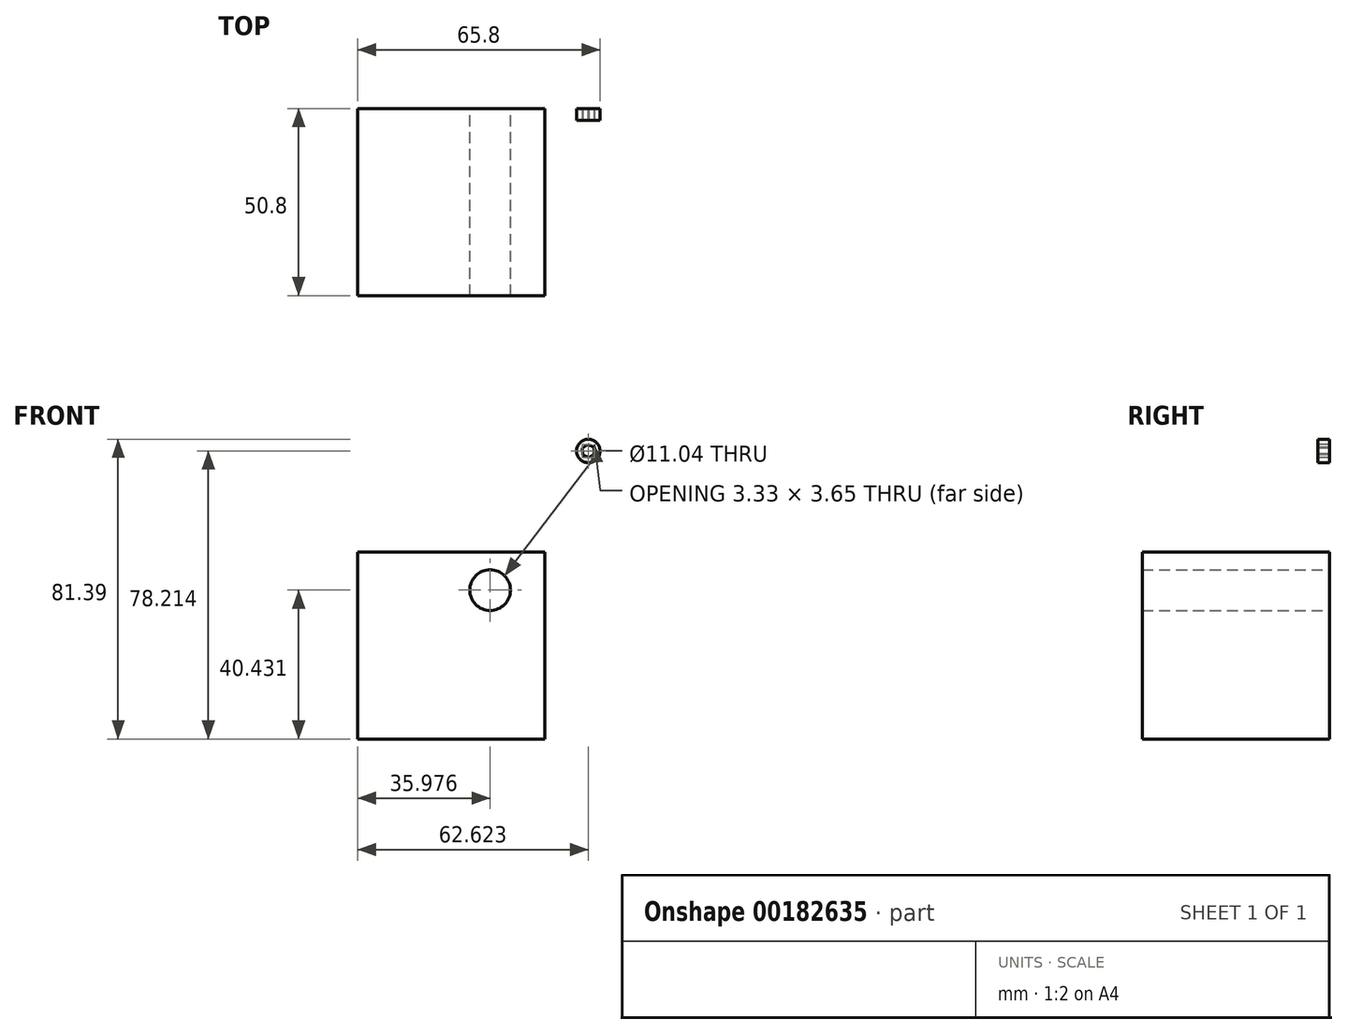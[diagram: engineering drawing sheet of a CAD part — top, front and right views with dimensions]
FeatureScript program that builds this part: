
annotation { "Feature Type Name" : "Feature", "Feature Type Description" : "" }
export const myFeature = defineFeature(function(context is Context, id is Id, definition is map)
    precondition{}
    {
        {
            var Q0;
            Q0=qCreatedBy(makeId("Front.planeOp"),FACE);
            var sketch = newSketch(context, id + "F0", { "sketchPlane" : qUnion([Q0])});
            skLineSegment(sketch, "E0", {"start": v(-24.42, 20.26) * mm, "end": v(26.38, 20.26) * mm});
            skLineSegment(sketch, "E1", {"start": v(26.38, 20.26) * mm, "end": v(26.38, -30.54) * mm});
            skLineSegment(sketch, "E2", {"start": v(26.38, -30.54) * mm, "end": v(-24.42, -30.54) * mm});
            skLineSegment(sketch, "E3", {"start": v(-24.42, 20.26) * mm, "end": v(-24.42, -30.54) * mm});
            skSolve(sketch);
        }
        {
            var Q0;
            Q0=makeQuery(id+"F0.imprint","IMPRINT",FACE,{"disambiguationData":[TD([[makeQuery(id+"F0.imprint","IMPRINT",EDGE,{"derivedFrom":sQuery(id+"F0.wireOp",EDGE,"E0")}),-1.0]])]});
            extrude(context, id + "F1", {"entities" : qUnion([Q0]), "depth" : 50.8 * mm});
        }
        {
            var Q0;
            Q0=makeQuery(id+"F0.imprint","IMPRINT",FACE,{"disambiguationData":[TD([[makeQuery(id+"F0.imprint","IMPRINT",EDGE,{"derivedFrom":sQuery(id+"F0.wireOp",EDGE,"E0")}),-1.0]])]});
            var sketch = newSketch(context, id + "F2", { "sketchPlane" : qUnion([Q0])});
            skCircle(sketch, "E4", {"center": v(11.56, 9.9) * mm, "radius": 5.52 * mm});
            skSolve(sketch);
        }
        {
            var Q0;
            Q0=makeQuery(id+"F2.imprint","IMPRINT",FACE,{"disambiguationData":[TD([[makeQuery(id+"F2.imprint","IMPRINT",EDGE,{"derivedFrom":sQuery(id+"F2.wireOp",EDGE,"E4")}),1.0]])]});
            extrude(context, id + "F3", {"entities" : qUnion([Q0]), "operationType" : NewBodyOperationType.REMOVE, "depth" : 50.8 * mm});
        }
        {
            var Q0;
            Q0=qCreatedBy(makeId("Front.planeOp"),FACE);
            var sketch = newSketch(context, id + "F4", { "sketchPlane" : qUnion([Q0])});
            skCircle(sketch, "E5", {"center": v(38.2, 47.67) * mm, "radius": 3.18 * mm});
            skSolve(sketch);
        }
        {
            var Q0;
            Q0=makeQuery(id+"F4.imprint","IMPRINT",FACE,{"disambiguationData":[TD([[makeQuery(id+"F4.imprint","IMPRINT",EDGE,{"derivedFrom":sQuery(id+"F4.wireOp",EDGE,"E5")}),1.0]])]});
            extrude(context, id + "F5", {"entities" : qUnion([Q0]), "depth" : 3.17 * mm});
        }
        {
            var Q0;
            Q0=makeQuery(id+"F5.opExtrude","CAP_FACE",FACE,{"disambiguationData":[OSD([sQuery(id+"F4.wireOp",EDGE,"E5")])],"isStart":false});
            var sketch = newSketch(context, id + "F6", { "sketchPlane" : qUnion([Q0])});
            skCircle(sketch, "E6.cCircle", {"center": v(38.2, 47.67) * mm, "radius": 1.59 * mm, "construction": true});
            skLineSegment(sketch, "E6.0", {"start": v(39.87, 46.91) * mm, "end": v(38.37, 45.85) * mm});
            skLineSegment(sketch, "E6.1", {"start": v(38.37, 45.85) * mm, "end": v(36.7, 46.61) * mm});
            skLineSegment(sketch, "E6.2", {"start": v(36.7, 46.61) * mm, "end": v(36.54, 48.44) * mm});
            skLineSegment(sketch, "E6.3", {"start": v(36.54, 48.44) * mm, "end": v(38.03, 49.5) * mm});
            skLineSegment(sketch, "E6.4", {"start": v(38.03, 49.5) * mm, "end": v(39.7, 48.74) * mm});
            skLineSegment(sketch, "E6.5", {"start": v(39.7, 48.74) * mm, "end": v(39.87, 46.91) * mm});
            skPoint(sketch, "E6.0.midPoint", {"position": v(39.12, 46.38) * mm});
            skSolve(sketch);
        }
        {
            var Q0;
            Q0 = qSketchRegion(id + "F6", true);
            var Q1;
            Q1=makeQuery(id+"F6.imprint","IMPRINT",FACE,{"disambiguationData":[TD([[makeQuery(id+"F6.imprint","IMPRINT",EDGE,{"derivedFrom":sQuery(id+"F6.wireOp",EDGE,"E6.0")}),-1.0]])]});
            extrude(context, id + "F7", {"entities" : qUnion([Q0, Q1]), "operationType" : NewBodyOperationType.REMOVE, "oppositeDirection" : true, "depth" : 3.17 * mm});
        }
    });
